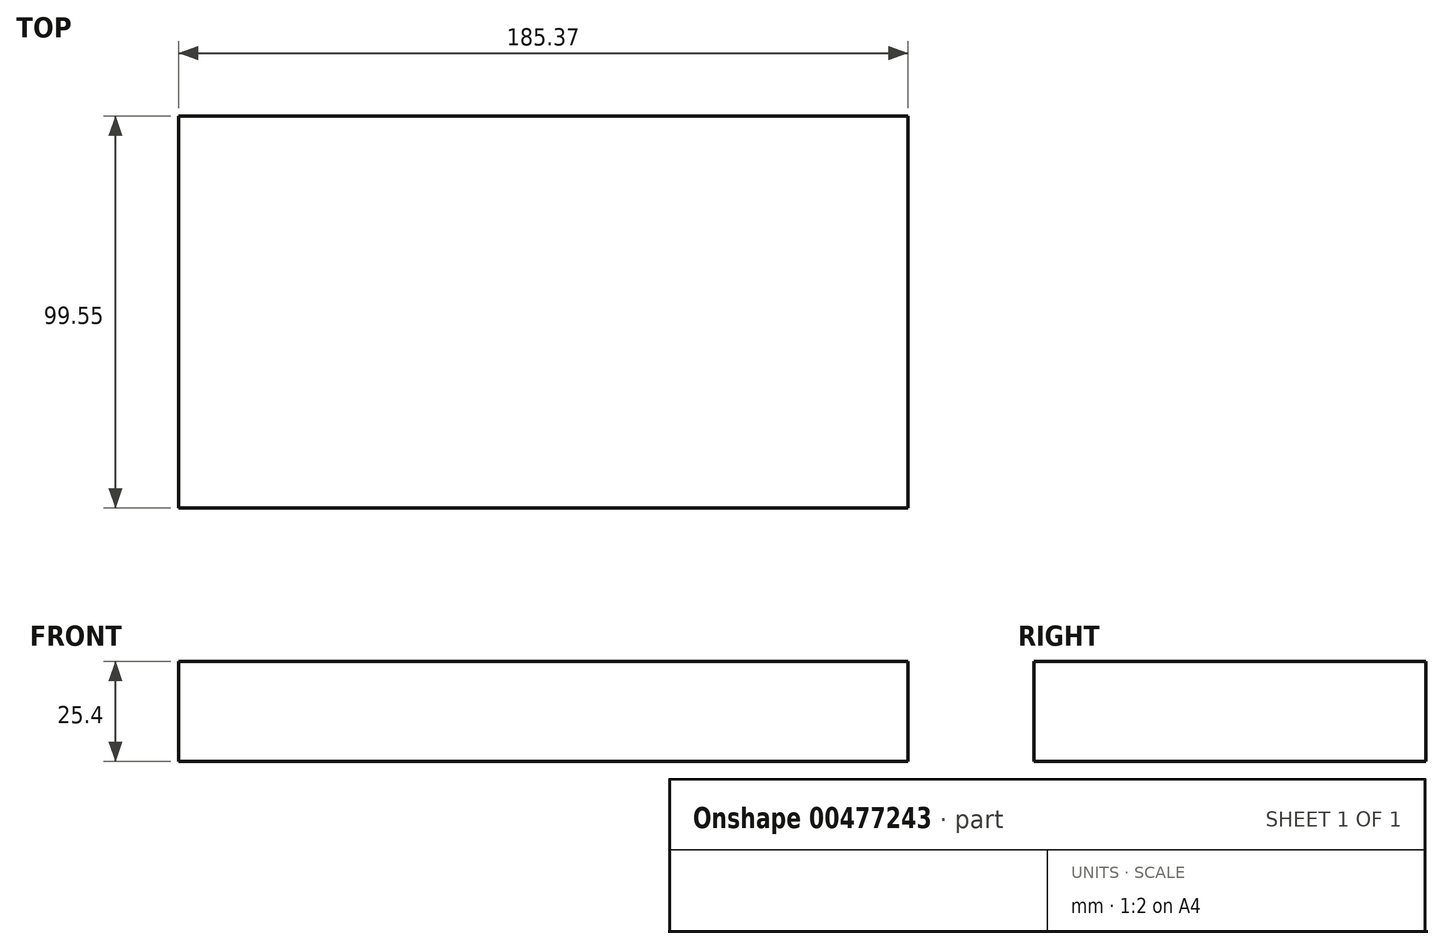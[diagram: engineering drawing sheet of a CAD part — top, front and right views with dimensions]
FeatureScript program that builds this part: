
annotation { "Feature Type Name" : "Feature", "Feature Type Description" : "" }
export const myFeature = defineFeature(function(context is Context, id is Id, definition is map)
    precondition{}
    {
        {
            var Q0;
            Q0=qCreatedBy(makeId("Top.planeOp"),FACE);
            var sketch = newSketch(context, id + "F0", { "sketchPlane" : qUnion([Q0])});
            skLineSegment(sketch, "E0.bottom", {"start": v(0, 0) * mm, "end": v(185.37, 0) * mm});
            skLineSegment(sketch, "E0.top", {"start": v(0, -99.55) * mm, "end": v(185.37, -99.55) * mm});
            skLineSegment(sketch, "E0.left", {"start": v(0, 0) * mm, "end": v(0, -99.55) * mm});
            skLineSegment(sketch, "E0.right", {"start": v(185.37, 0) * mm, "end": v(185.37, -99.55) * mm});
            skSolve(sketch);
        }
        {
            var Q0;
            Q0 = qSketchRegion(id + "F0", true);
            extrude(context, id + "F1", {"entities" : qUnion([Q0]), "depth" : 25.4 * mm});
        }
        {
            var Q0;
            Q0=qCreatedBy(makeId("Top.planeOp"),FACE);
            var sketch = newSketch(context, id + "F2", { "sketchPlane" : qUnion([Q0])});
            skCircle(sketch, "E1", {"center": v(71.48, 40.64) * mm, "radius": 38.1 * mm});
            skSolve(sketch);
        }
        {
            var Q0;
            Q0=makeQuery(id+"F2.imprint","IMPRINT",FACE,{"disambiguationData":[TD([[makeQuery(id+"F2.imprint","IMPRINT",EDGE,{"derivedFrom":sQuery(id+"F2.wireOp",EDGE,"E1")}),1.0]])]});
            extrude(context, id + "F3", {"entities" : qUnion([Q0]), "operationType" : NewBodyOperationType.REMOVE, "depth" : 41.66 * mm, "hasDraft" : true, "draftAngle" : 3 * degree});
        }
    });
